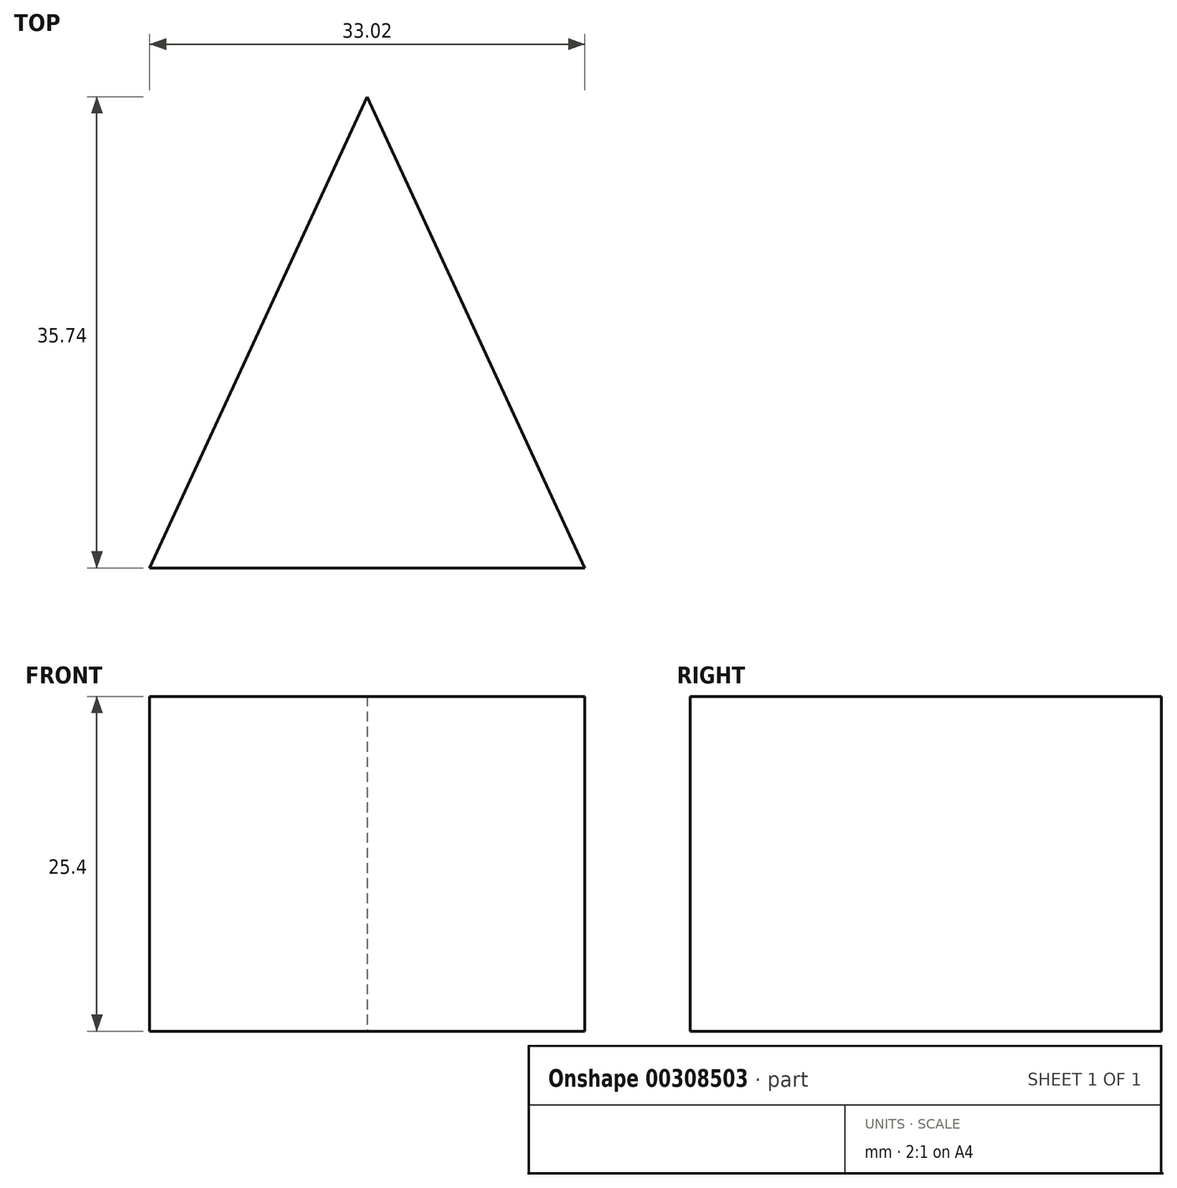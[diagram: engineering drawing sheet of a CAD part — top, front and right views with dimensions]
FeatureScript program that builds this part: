
annotation { "Feature Type Name" : "Feature", "Feature Type Description" : "" }
export const myFeature = defineFeature(function(context is Context, id is Id, definition is map)
    precondition{}
    {
        {
            var Q0;
            Q0=qCreatedBy(makeId("Top.planeOp"),FACE);
            var sketch = newSketch(context, id + "F0", { "sketchPlane" : qUnion([Q0])});
            skLineSegment(sketch, "E0", {"start": v(-16.51, 0) * mm, "end": v(16.5, 0) * mm});
            skLineSegment(sketch, "E1", {"start": v(-16.51, 0) * mm, "end": v(0, 35.74) * mm});
            skLineSegment(sketch, "E2", {"start": v(0, 35.74) * mm, "end": v(16.5, 0) * mm});
            skSolve(sketch);
        }
        {
            var Q0;
            Q0=makeQuery(id+"F0.imprint","IMPRINT",FACE,{"disambiguationData":[TD([[makeQuery(id+"F0.imprint","IMPRINT",EDGE,{"derivedFrom":sQuery(id+"F0.wireOp",EDGE,"E0")}),1.0]])]});
            extrude(context, id + "F1", {"entities" : qUnion([Q0]), "depth" : 25.4 * mm});
        }
    });
